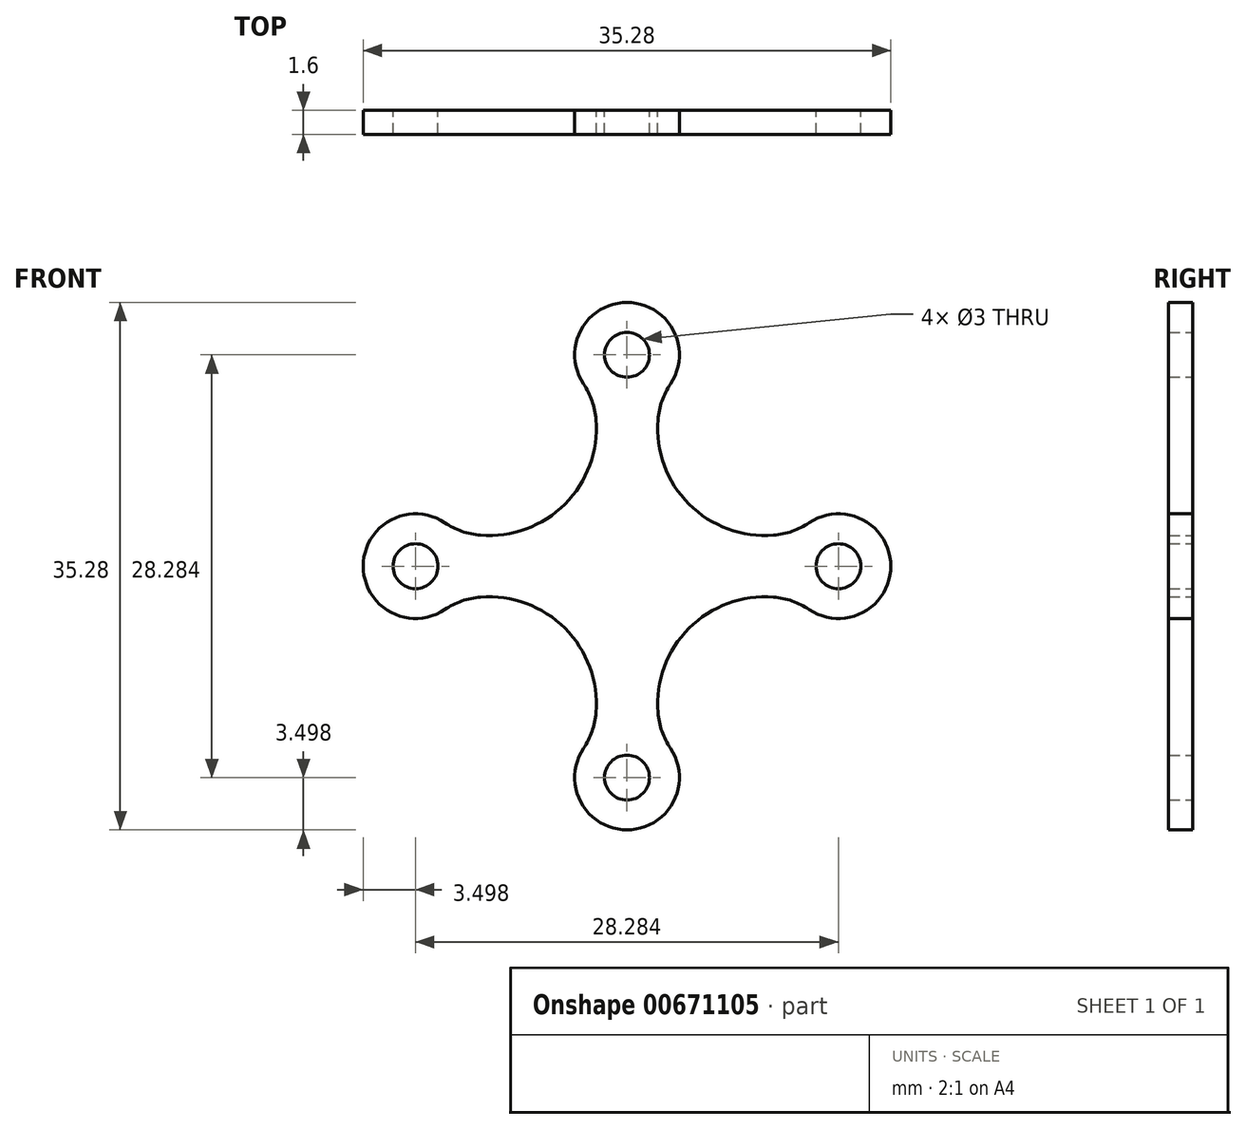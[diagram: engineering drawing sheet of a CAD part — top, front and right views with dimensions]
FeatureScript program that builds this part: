
annotation { "Feature Type Name" : "Feature", "Feature Type Description" : "" }
export const myFeature = defineFeature(function(context is Context, id is Id, definition is map)
    precondition{}
    {
        {
            var Q0;
            Q0=qCreatedBy(makeId("Front.planeOp"),FACE);
            var sketch = newSketch(context, id + "F0", { "sketchPlane" : qUnion([Q0])});
            skPoint(sketch, "E0.middle", {"position": v(0, 0) * mm});
            skCircle(sketch, "E1", {"center": v(0, 14.14) * mm, "radius": 1.5 * mm});
            skCircle(sketch, "E2", {"center": v(14.14, 0) * mm, "radius": 1.5 * mm});
            skCircle(sketch, "E3", {"center": v(0, -14.14) * mm, "radius": 1.5 * mm});
            skCircle(sketch, "E4", {"center": v(-14.14, 0) * mm, "radius": 1.5 * mm});
            skArc(sketch, "E5.0", {"start": v(-12.19, 2.9) * mm, "mid": v(-17.64, 0) * mm, "end": v(-12.19, -2.9) * mm});
            skArc(sketch, "E6.0", {"start": v(2.9, 12.19) * mm, "mid": v(0, 17.64) * mm, "end": v(-2.9, 12.19) * mm});
            skArc(sketch, "E7.0", {"start": v(-2.9, -12.19) * mm, "mid": v(0, -17.64) * mm, "end": v(2.9, -12.19) * mm});
            skArc(sketch, "E8.0", {"start": v(12.19, -2.9) * mm, "mid": v(17.64, 0) * mm, "end": v(12.19, 2.9) * mm});
            skArc(sketch, "E9", {"start": v(-2.07, -9.8) * mm, "mid": v(-4.15, -4.15) * mm, "end": v(-9.8, -2.07) * mm});
            skArc(sketch, "E10.MirrorCS", {"start": v(-2.07, 9.8) * mm, "mid": v(-4.15, 4.15) * mm, "end": v(-9.8, 2.07) * mm});
            skArc(sketch, "E11.MirrorCS", {"start": v(2.07, 9.8) * mm, "mid": v(4.15, 4.15) * mm, "end": v(9.8, 2.07) * mm});
            skArc(sketch, "E12.MirrorCS", {"start": v(2.07, -9.8) * mm, "mid": v(4.15, -4.15) * mm, "end": v(9.8, -2.07) * mm});
            skPoint(sketch, "E13.visualSharp", {"position": v(-2.47, -11.67) * mm});
            skArc(sketch, "E13.filletArc", {"start": v(-2.9, -12.19) * mm, "mid": v(-2.33, -11.05) * mm, "end": v(-2.07, -9.8) * mm});
            skPoint(sketch, "E14.visualSharp", {"position": v(2.47, -11.67) * mm});
            skArc(sketch, "E14.filletArc", {"start": v(2.07, -9.8) * mm, "mid": v(2.33, -11.05) * mm, "end": v(2.9, -12.19) * mm});
            skPoint(sketch, "E15.visualSharp", {"position": v(-11.67, -2.47) * mm});
            skArc(sketch, "E15.filletArc", {"start": v(-9.8, -2.07) * mm, "mid": v(-11.05, -2.33) * mm, "end": v(-12.19, -2.9) * mm});
            skPoint(sketch, "E16.visualSharp", {"position": v(-11.67, 2.47) * mm});
            skArc(sketch, "E16.filletArc", {"start": v(-12.19, 2.9) * mm, "mid": v(-11.05, 2.33) * mm, "end": v(-9.8, 2.07) * mm});
            skPoint(sketch, "E17.visualSharp", {"position": v(-2.47, 11.67) * mm});
            skArc(sketch, "E17.filletArc", {"start": v(-2.07, 9.8) * mm, "mid": v(-2.33, 11.05) * mm, "end": v(-2.9, 12.19) * mm});
            skPoint(sketch, "E18.visualSharp", {"position": v(2.47, 11.67) * mm});
            skArc(sketch, "E18.filletArc", {"start": v(2.9, 12.19) * mm, "mid": v(2.33, 11.05) * mm, "end": v(2.07, 9.8) * mm});
            skPoint(sketch, "E19.visualSharp", {"position": v(11.67, -2.47) * mm});
            skArc(sketch, "E19.filletArc", {"start": v(12.19, -2.9) * mm, "mid": v(11.05, -2.33) * mm, "end": v(9.8, -2.07) * mm});
            skPoint(sketch, "E20.visualSharp", {"position": v(11.67, 2.47) * mm});
            skArc(sketch, "E20.filletArc", {"start": v(9.8, 2.07) * mm, "mid": v(11.05, 2.33) * mm, "end": v(12.19, 2.9) * mm});
            skSolve(sketch);
        }
        {
            var Q0;
            Q0=makeQuery(id+"F0.imprint","IMPRINT",FACE,{"disambiguationData":[TD([[makeQuery(id+"F0.imprint","IMPRINT",EDGE,{"derivedFrom":sQuery(id+"F0.wireOp",EDGE,"E1")}),-1.0]])]});
            extrude(context, id + "F1", {"entities" : qUnion([Q0]), "depth" : 1.6 * mm, "offsetDistance" : 25 * mm});
        }
    });
